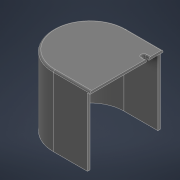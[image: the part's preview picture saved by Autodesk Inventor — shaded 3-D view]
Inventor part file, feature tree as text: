
AUTODESK INVENTOR PART (.ipt)
format: ipt  version: 2022 (Build 260153000, 153)  size: 297,984 bytes
history: native  units: mm
features: extrude x3, sketch x3, fillet x1
ambient origin geometry x8: Origin, YZ Plane, XZ Plane, XY Plane, X Axis, Y Axis, Z Axis, Center Point
bodies: Solid1 (feature_tree)
feature tree (7):
  extrude  "Extrusion1"  Depth=80.0mm TaperAngle=0.0deg
  extrude  "Extrusion2"  Depth=3.0mm TaperAngle=0.0deg
  extrude  "Extrusion3"  [1 undecoded]
  fillet  "Fillet1"  [1 undecoded]
  sketch  "Sketch1"  dims[d7=3.0mm d10=80.0mm d11=0.0mm]
  sketch  "Sketch2"  dims[d15=3.0mm d16=0.0mm d19=3.0mm d20=0.0mm]
  sketch  "Sketch3"  dims[d21=2.0mm]
note: 2 required parameter values undecoded (feature->parameter linkage not recoverable at this tier; creation-order binding heuristic only, values carry confidence <= 0.55)
